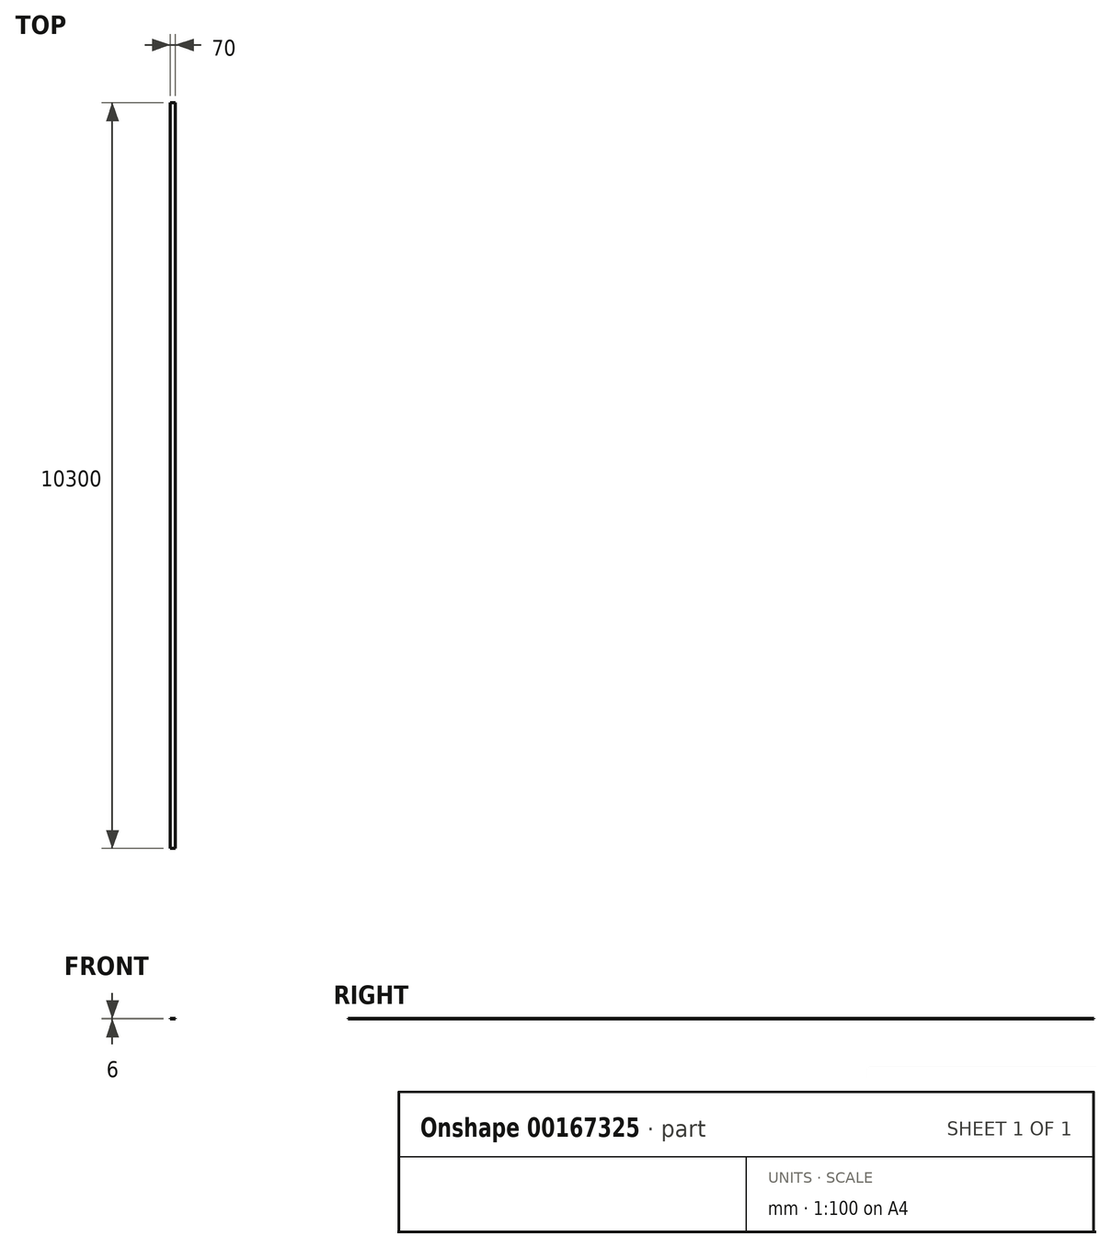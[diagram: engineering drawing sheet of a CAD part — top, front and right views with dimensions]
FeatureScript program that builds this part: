
annotation { "Feature Type Name" : "Feature", "Feature Type Description" : "" }
export const myFeature = defineFeature(function(context is Context, id is Id, definition is map)
    precondition{}
    {
        {
            var Q0;
            Q0=qCreatedBy(makeId("Front.planeOp"),FACE);
            var sketch = newSketch(context, id + "F0", { "sketchPlane" : qUnion([Q0])});
            skLineSegment(sketch, "E0.bottom", {"start": v(0, 0) * mm, "end": v(70, 0) * mm});
            skLineSegment(sketch, "E0.top", {"start": v(0, 6) * mm, "end": v(70, 6) * mm});
            skLineSegment(sketch, "E0.left", {"start": v(0, 0) * mm, "end": v(0, 6) * mm});
            skLineSegment(sketch, "E0.right", {"start": v(70, 0) * mm, "end": v(70, 6) * mm});
            skSolve(sketch);
        }
        {
            var Q0;
            Q0 = qSketchRegion(id + "F0", true);
            extrude(context, id + "F1", {"entities" : qUnion([Q0]), "depth" : 10300 * mm});
        }
    });
